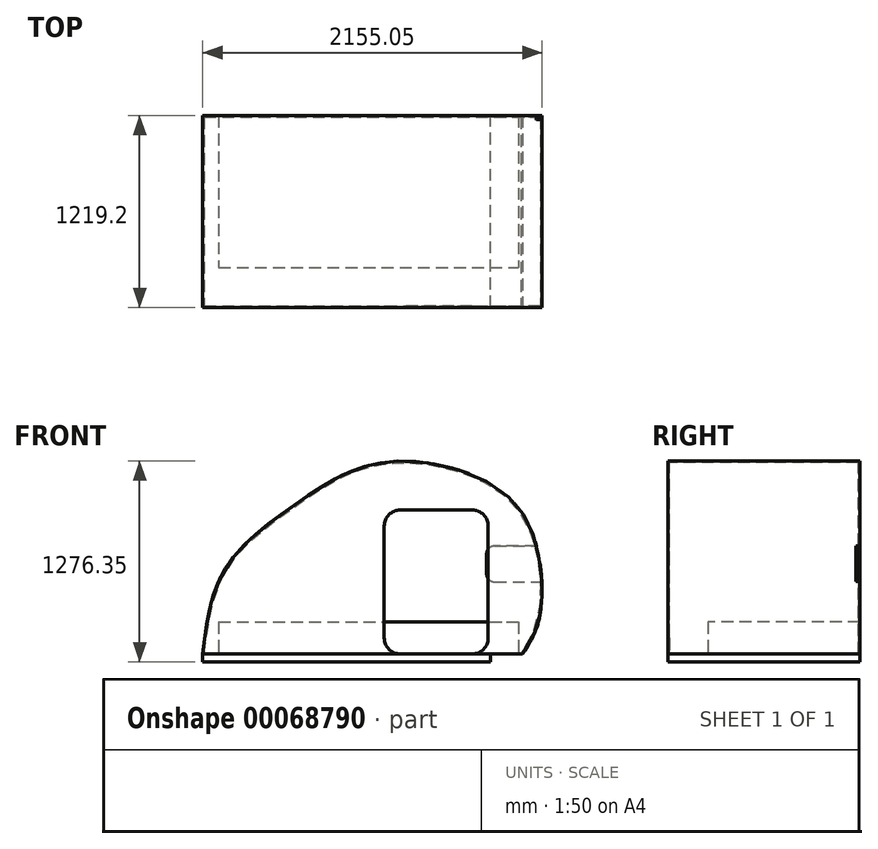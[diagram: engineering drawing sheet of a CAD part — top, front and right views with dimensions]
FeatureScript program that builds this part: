
annotation { "Feature Type Name" : "Feature", "Feature Type Description" : "" }
export const myFeature = defineFeature(function(context is Context, id is Id, definition is map)
    precondition{}
    {
        {
            var Q0;
            Q0=qCreatedBy(makeId("Top.planeOp"),FACE);
            var sketch = newSketch(context, id + "F0", { "sketchPlane" : qUnion([Q0])});
            skLineSegment(sketch, "E0.bottom", {"start": v(0, 0) * mm, "end": v(1828.8, 0) * mm});
            skLineSegment(sketch, "E0.top", {"start": v(0, 1219.2) * mm, "end": v(1828.8, 1219.2) * mm});
            skLineSegment(sketch, "E0.left", {"start": v(0, 0) * mm, "end": v(0, 1219.2) * mm});
            skLineSegment(sketch, "E0.right", {"start": v(1828.8, 0) * mm, "end": v(1828.8, 1219.2) * mm});
            skSolve(sketch);
        }
        {
            var Q0;
            Q0 = qSketchRegion(id + "F0", true);
            extrude(context, id + "F1", {"entities" : qUnion([Q0]), "depth" : 50.8 * mm});
        }
        {
            var Q0;
            Q0=makeQuery(id+"F1.opExtrude","SWEPT_FACE",FACE,{"disambiguationData":[OSD([sQuery(id+"F0.wireOp",EDGE,"E0.bottom")])]});
            var sketch = newSketch(context, id + "F2", { "sketchPlane" : qUnion([Q0])});
            skLineSegment(sketch, "E1", {"start": v(0, 50.8) * mm, "end": v(2032, 50.8) * mm});
            skFitSpline(sketch, "E2", {"points": [v(0, 50.8) * mm, v(134.09, 579.23) * mm, v(581.8, 996.8) * mm, v(1162.51, 1270) * mm, v(1888.1, 1092.96) * mm, v(2120.52, 736.33) * mm, v(2152.58, 383.7) * mm, v(2032, 50.8) * mm], "startDerivative": vector(462.64, 3704.8) * mm, "endDerivative": vector(-2318.31, -3414.99) * mm});
            skSolve(sketch);
        }
        {
            var Q0;
            Q0 = qSketchRegion(id + "F2", true);
            extrude(context, id + "F3", {"entities" : qUnion([Q0]), "oppositeDirection" : true, "depth" : 1219.2 * mm});
        }
        {
            var Q0;
            Q0=makeQuery(id+"F3.opExtrude","SWEPT_FACE",FACE,{"disambiguationData":[OSD([sQuery(id+"F2.wireOp",EDGE,"E1")])]});
            shell(context, id + "F4", {"entities" : qUnion([Q0]), "thickness" : 9.52 * mm});
        }
        {
            var Q0;
            Q0=makeQuery(id+"F3.opExtrude","CAP_FACE",FACE,{"disambiguationData":[OSD([sQuery(id+"F2.wireOp",EDGE,"E1"),sQuery(id+"F2.wireOp",EDGE,"E2")])],"isStart":true});
            var sketch = newSketch(context, id + "F5", { "sketchPlane" : qUnion([Q0])});
            skLineSegment(sketch, "E3.bottom", {"start": v(1711.68, 50.8) * mm, "end": v(1254.48, 50.8) * mm});
            skLineSegment(sketch, "E3.top", {"start": v(1711.68, 965.2) * mm, "end": v(1254.48, 965.2) * mm});
            skLineSegment(sketch, "E3.left", {"start": v(1813.28, 152.4) * mm, "end": v(1813.28, 863.6) * mm});
            skLineSegment(sketch, "E3.right", {"start": v(1152.88, 152.4) * mm, "end": v(1152.88, 863.6) * mm});
            skPoint(sketch, "E4.visualSharp", {"position": v(1152.88, 965.2) * mm});
            skArc(sketch, "E4.filletArc", {"start": v(1254.48, 965.2) * mm, "mid": v(1182.64, 935.44) * mm, "end": v(1152.88, 863.6) * mm});
            skPoint(sketch, "E5.visualSharp", {"position": v(1813.28, 965.2) * mm});
            skArc(sketch, "E5.filletArc", {"start": v(1813.28, 863.6) * mm, "mid": v(1783.52, 935.44) * mm, "end": v(1711.68, 965.2) * mm});
            skPoint(sketch, "E6.visualSharp", {"position": v(1152.88, 50.8) * mm});
            skArc(sketch, "E6.filletArc", {"start": v(1152.88, 152.4) * mm, "mid": v(1182.64, 80.56) * mm, "end": v(1254.48, 50.8) * mm});
            skPoint(sketch, "E7.visualSharp", {"position": v(1813.28, 50.8) * mm});
            skArc(sketch, "E7.filletArc", {"start": v(1711.68, 50.8) * mm, "mid": v(1783.52, 80.56) * mm, "end": v(1813.28, 152.4) * mm});
            skSolve(sketch);
        }
        {
            var Q0;
            Q0 = qSketchRegion(id + "F5", true);
            extrude(context, id + "F6", {"entities" : qUnion([Q0]), "operationType" : NewBodyOperationType.REMOVE, "oppositeDirection" : true, "depth" : 25.4 * mm});
        }
        {
            var Q0;
            Q0=makeQuery(id+"F3.opExtrude","CAP_FACE",FACE,{"disambiguationData":[OSD([sQuery(id+"F2.wireOp",EDGE,"E1"),sQuery(id+"F2.wireOp",EDGE,"E2")])],"isStart":false});
            var sketch = newSketch(context, id + "F7", { "sketchPlane" : qUnion([Q0])});
            skLineSegment(sketch, "E8.bottom", {"start": v(-2133.6, 736.6) * mm, "end": v(-1854.2, 736.6) * mm});
            skLineSegment(sketch, "E8.top", {"start": v(-2133.6, 508) * mm, "end": v(-1854.2, 508) * mm});
            skLineSegment(sketch, "E8.left", {"start": v(-2184.4, 685.8) * mm, "end": v(-2184.4, 558.8) * mm});
            skLineSegment(sketch, "E8.right", {"start": v(-1803.4, 685.8) * mm, "end": v(-1803.4, 558.8) * mm});
            skPoint(sketch, "E9.visualSharp", {"position": v(-2184.4, 736.6) * mm});
            skArc(sketch, "E9.filletArc", {"start": v(-2133.6, 736.6) * mm, "mid": v(-2169.52, 721.72) * mm, "end": v(-2184.4, 685.8) * mm});
            skPoint(sketch, "E10.visualSharp", {"position": v(-1803.4, 736.6) * mm});
            skArc(sketch, "E10.filletArc", {"start": v(-1803.4, 685.8) * mm, "mid": v(-1818.28, 721.72) * mm, "end": v(-1854.2, 736.6) * mm});
            skPoint(sketch, "E11.visualSharp", {"position": v(-2184.4, 508) * mm});
            skArc(sketch, "E11.filletArc", {"start": v(-2184.4, 558.8) * mm, "mid": v(-2169.52, 522.88) * mm, "end": v(-2133.6, 508) * mm});
            skPoint(sketch, "E12.visualSharp", {"position": v(-1803.4, 508) * mm});
            skArc(sketch, "E12.filletArc", {"start": v(-1854.2, 508) * mm, "mid": v(-1818.28, 522.88) * mm, "end": v(-1803.4, 558.8) * mm});
            skSolve(sketch);
        }
        {
            var Q0;
            Q0 = qSketchRegion(id + "F7", true);
            extrude(context, id + "F8", {"entities" : qUnion([Q0]), "operationType" : NewBodyOperationType.REMOVE, "oppositeDirection" : true, "depth" : 25.4 * mm});
        }
        {
            var Q0;
            Q0=makeQuery(id+"F1.opExtrude","CAP_FACE",FACE,{"disambiguationData":[OSD([sQuery(id+"F0.wireOp",EDGE,"E0.bottom"),sQuery(id+"F0.wireOp",EDGE,"E0.top"),sQuery(id+"F0.wireOp",EDGE,"E0.left"),sQuery(id+"F0.wireOp",EDGE,"E0.right")])],"isStart":false});
            var sketch = newSketch(context, id + "F9", { "sketchPlane" : qUnion([Q0])});
            skLineSegment(sketch, "E13.bottom", {"start": v(101.6, 1219.2) * mm, "end": v(2006.6, 1219.2) * mm});
            skLineSegment(sketch, "E13.top", {"start": v(101.6, 254) * mm, "end": v(2006.6, 254) * mm});
            skLineSegment(sketch, "E13.left", {"start": v(101.6, 1219.2) * mm, "end": v(101.6, 254) * mm});
            skLineSegment(sketch, "E13.right", {"start": v(2006.6, 1219.2) * mm, "end": v(2006.6, 254) * mm});
            skSolve(sketch);
        }
        {
            var Q0;
            Q0 = qSketchRegion(id + "F9", true);
            extrude(context, id + "F10", {"entities" : qUnion([Q0]), "depth" : 203.2 * mm});
        }
    });
